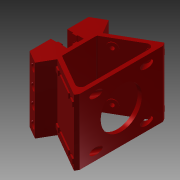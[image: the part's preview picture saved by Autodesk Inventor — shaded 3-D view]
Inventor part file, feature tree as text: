
AUTODESK INVENTOR PART (.ipt)
format: ipt  version: 2015 SP1 (Build 190203100, 203)  size: 563,200 bytes
history: native  units: mm
features: sketch x15, extrude x11, plane x4, hole x4, fillet x2
ambient origin geometry x8: Origin, YZ Plane, XZ Plane, XY Plane, X Axis, Y Axis, Z Axis, Center Point
bodies: Solid2 (feature_tree)
feature tree (36):
  extrude  "Extrusion13"  Depth=55.0mm
  fillet  "Fillet5"  Radius=20.0mm
  extrude  "Extrusion2"  Depth=2.0mm
  extrude  "Extrusion7"  Depth=2.0mm
  plane  "Work Plane20"
  hole  "Hole2"  [1 undecoded]
  plane  "Work Plane21"
  hole  "Hole3"  [1 undecoded]
  plane  "Work Plane18"
  hole  "Hole7"  [1 undecoded]
  plane  "Work Plane19"
  hole  "Hole8"  [1 undecoded]
  extrude  "Extrusion14"  Depth=5.5mm
  extrude  "Extrusion15"  Depth=5.5mm
  fillet  "Fillet6"  Radius=3.0mm
  extrude  "Extrusion16"  TaperAngle=60.0deg  [1 undecoded]
  extrude  "Extrusion17"  TaperAngle=60.0deg  [1 undecoded]
  extrude  "Extrusion18"  Depth=20.0mm
  extrude  "Extrusion19"  Depth=20.0mm
  extrude  "Extrusion20"  Depth=6.25mm
  extrude  "Extrusion21"  Depth=20.0mm
  sketch  "Sketch1"  dims[d11=20.0mm d12=55.0mm d19=20.0mm]
  sketch  "Sketch2"  dims[d23=6.0mm d24=2.0mm]
  sketch  "Sketch8"  dims[d25=6.0mm d26=2.0mm]
  sketch  "Sketch9"  dims[d27=60.0mm d28=0.0mm d63=8.0mm d64=0.0mm]
  sketch  "Sketch10"  dims[d65=4.5mm d66=6.0mm d67=8.0mm d68=32.0mm d69=90.0deg d70=30.0mm d71=20.594885mm d73=35.0mm]
  sketch  "Sketch20"  dims[d74=35.0mm]
  sketch  "Sketch21"  dims[d78=4.5mm d79=6.0mm d80=8.0mm d81=32.0mm d82=90.0deg d83=8.0mm d84=20.594885mm d110=42.5mm]
  sketch  "Sketch22"  dims[d166=80.0mm d167=0.0mm d168=20.0mm]
  sketch  "Sketch23"  dims[d169=20.0mm d171=5.5mm]
  sketch  "Sketch24"  dims[d172=3.0mm d173=5.5mm d174=3.0mm]
  sketch  "Sketch26"  dims[d176=5.0mm d177=60.0deg]
  sketch  "Sketch27"  dims[d178=120.0deg d179=60.0deg]
  sketch  "Sketch28"  dims[d181=20.0mm d184=1.5mm]
  sketch  "Sketch29"  dims[d185=5.5mm d186=20.0mm]
  sketch  "Sketch30"  dims[d188=4.5mm d189=6.0mm d190=8.0mm d191=16.35mm d192=90.0deg d193=8.0mm d194=20.594885mm d195=34.865485mm d196=20.0mm d197=4.5mm d198=6.0mm d199=8.0mm d200=16.35mm d201=90.0deg d202=8.0mm d203=20.594885mm d204=33.0mm d205=10.0mm d206=5.0mm d207=33.0mm d208=10.0mm d209=55.0mm d210=20.0mm d211=20.0mm d212=20.0mm d213=20.0mm d214=20.0mm d215=50.0mm d216=10.0mm d217=0.0mm d218=15.0mm d219=10.0mm d220=0.0mm d221=2.0mm d222=12.0mm d223=12.0mm d224=1.0mm d225=0.0mm d228=12.0mm d229=12.0mm d230=12.0mm d231=12.0mm d232=12.0mm d233=12.0mm d234=1.0mm d235=0.0mm d236=6.25mm d237=6.25mm d238=6.25mm d239=6.25mm d240=6.25mm d241=6.25mm d242=6.25mm d243=6.25mm d244=1.0mm d245=0.0mm d246=6.25mm d247=6.25mm d248=6.25mm d249=6.25mm d250=6.25mm d251=6.25mm d252=6.25mm d253=6.25mm d254=1.0mm d255=0.0mm d256=6.25mm d257=6.25mm d258=6.25mm d259=6.25mm d260=6.25mm d261=6.25mm d262=6.25mm d263=6.25mm d264=1.0mm d265=0.0mm d266=6.25mm d267=6.25mm d268=6.25mm d269=6.25mm d270=6.25mm d271=6.25mm d272=6.25mm d273=6.25mm d274=1.0mm d275=0.0mm]
note: 6 required parameter values undecoded (feature->parameter linkage not recoverable at this tier; creation-order binding heuristic only, values carry confidence <= 0.55)
